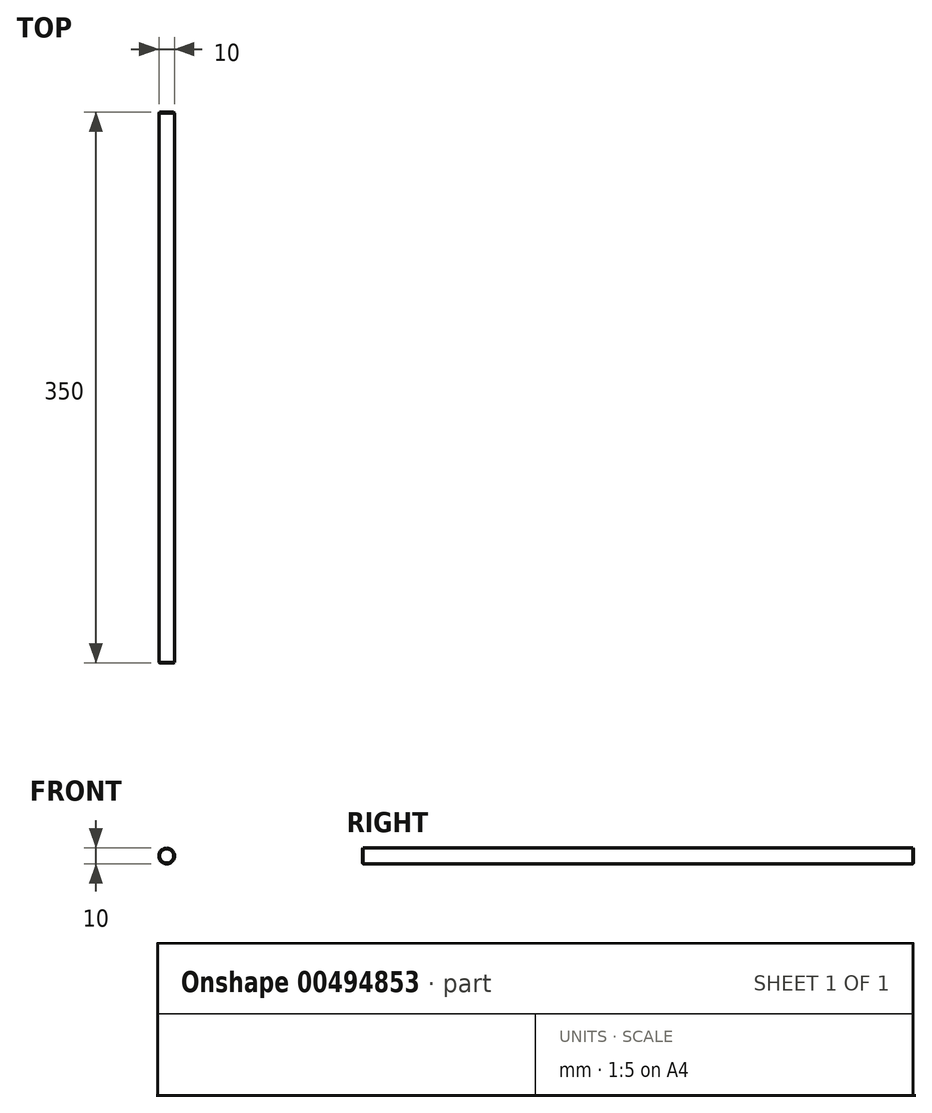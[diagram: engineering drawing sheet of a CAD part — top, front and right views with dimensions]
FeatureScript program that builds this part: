
annotation { "Feature Type Name" : "Feature", "Feature Type Description" : "" }
export const myFeature = defineFeature(function(context is Context, id is Id, definition is map)
    precondition{}
    {
        {
            var Q0;
            Q0=qCreatedBy(makeId("Front.planeOp"),FACE);
            var sketch = newSketch(context, id + "F0", { "sketchPlane" : qUnion([Q0])});
            skCircle(sketch, "E0", {"center": v(0, 0) * mm, "radius": 5 * mm});
            skSolve(sketch);
        }
        {
            var Q0;
            Q0=qSketchRegion(id+"F0",true);
            extrude(context, id + "F1", {"entities" : qUnion([Q0]), "depth" : 350 * mm});
        }
        {
            var Q0;
            Q0=makeQuery(id+"F1.opExtrude","CAP_EDGE",EDGE,{"disambiguationData":[OSD([sQuery(id+"F0.wireOp",EDGE,"E0")])],"isStart":true});
            var Q1;
            Q1=makeQuery(id+"F1.opExtrude","CAP_EDGE",EDGE,{"disambiguationData":[OSD([sQuery(id+"F0.wireOp",EDGE,"E0")])],"isStart":false});
            chamfer(context, id + "F2", {"entities" : qUnion([Q0, Q1]), "width" : 0.5 * mm, "tangentPropagation" : true});
        }
    });
